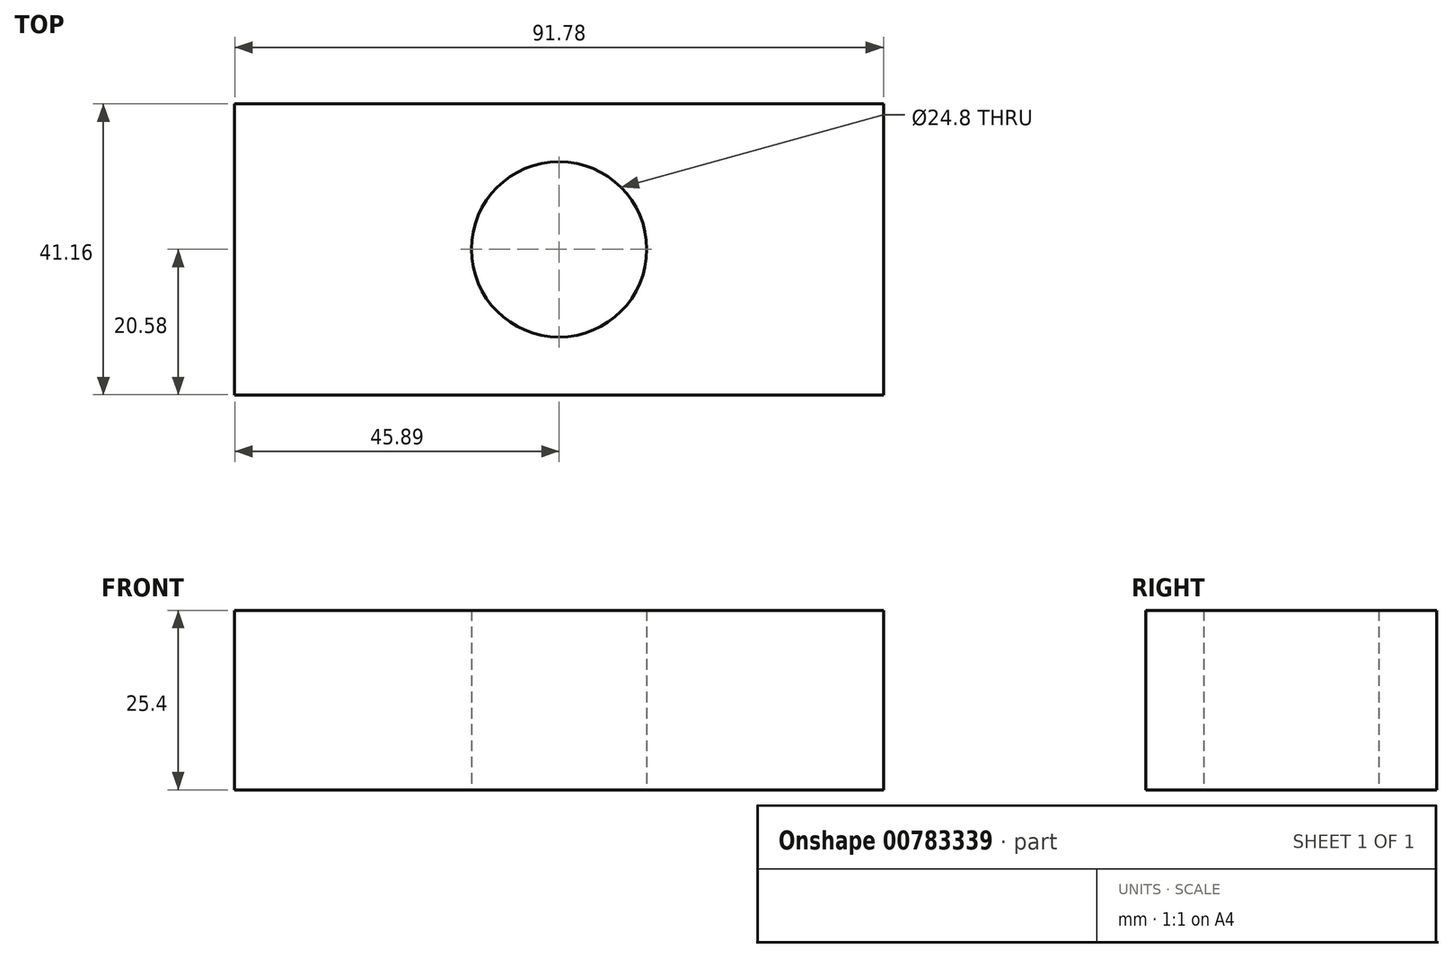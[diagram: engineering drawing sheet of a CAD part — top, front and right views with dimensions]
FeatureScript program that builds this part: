
annotation { "Feature Type Name" : "Feature", "Feature Type Description" : "" }
export const myFeature = defineFeature(function(context is Context, id is Id, definition is map)
    precondition{}
    {
        {
            var Q0;
            Q0=qCreatedBy(makeId("Top.planeOp"),FACE);
            var sketch = newSketch(context, id + "F0", { "sketchPlane" : qUnion([Q0])});
            skLineSegment(sketch, "E0.bottom", {"start": v(45.9, -20.58) * mm, "end": v(-45.9, -20.58) * mm});
            skLineSegment(sketch, "E0.top", {"start": v(45.9, 20.58) * mm, "end": v(-45.9, 20.58) * mm});
            skLineSegment(sketch, "E0.left", {"start": v(45.9, -20.58) * mm, "end": v(45.9, 20.58) * mm});
            skLineSegment(sketch, "E0.right", {"start": v(-45.9, -20.58) * mm, "end": v(-45.9, 20.58) * mm});
            skPoint(sketch, "E0.middle", {"position": v(0, 0) * mm});
            skCircle(sketch, "E1", {"center": v(0, 0) * mm, "radius": 12.4 * mm});
            skSolve(sketch);
        }
        {
            var Q0;
            Q0=makeQuery(id+"F0.imprint","IMPRINT",FACE,{"disambiguationData":[TD([[makeQuery(id+"F0.imprint","IMPRINT",EDGE,{"derivedFrom":sQuery(id+"F0.wireOp",EDGE,"E0.bottom")}),-1.0]])]});
            extrude(context, id + "F1", {"entities" : qUnion([Q0]), "depth" : 25.4 * mm, "offsetDistance" : 25.4 * mm});
        }
    });
